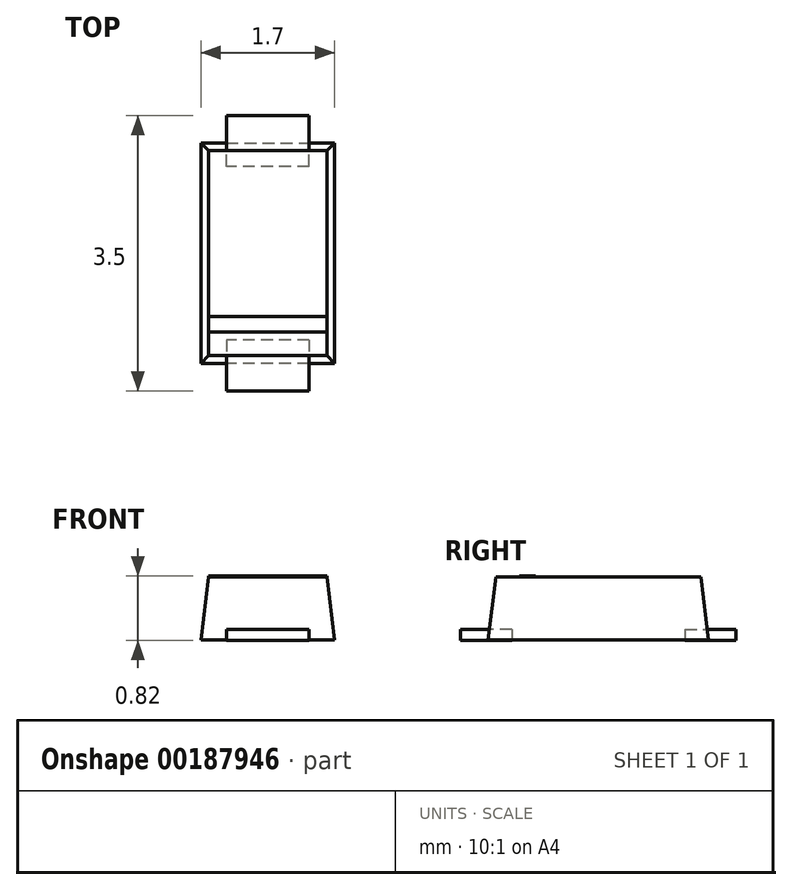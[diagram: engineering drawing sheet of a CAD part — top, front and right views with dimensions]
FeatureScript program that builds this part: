
annotation { "Feature Type Name" : "Feature", "Feature Type Description" : "" }
export const myFeature = defineFeature(function(context is Context, id is Id, definition is map)
    precondition{}
    {
        {
            var Q0;
            Q0=qCreatedBy(makeId("Top.planeOp"),FACE);
            var sketch = newSketch(context, id + "F0", { "sketchPlane" : qUnion([Q0])});
            skLineSegment(sketch, "E0.bottom", {"start": v(0.85, -1.4) * mm, "end": v(-0.85, -1.4) * mm});
            skLineSegment(sketch, "E0.top", {"start": v(0.85, 1.4) * mm, "end": v(-0.85, 1.4) * mm});
            skLineSegment(sketch, "E0.left", {"start": v(0.85, -1.4) * mm, "end": v(0.85, 1.4) * mm});
            skLineSegment(sketch, "E0.right", {"start": v(-0.85, -1.4) * mm, "end": v(-0.85, 1.4) * mm});
            skPoint(sketch, "E0.middle", {"position": v(0, 0) * mm});
            skSolve(sketch);
        }
        {
            var Q0;
            Q0=qSketchRegion(id+"F0",true);
            extrude(context, id + "F1", {"entities" : qUnion([Q0]), "depth" : 0.8 * mm, "hasDraft" : true, "draftAngle" : 7 * degree, "draftPullDirection" : true});
        }
        {
            var Q0;
            Q0=qCreatedBy(makeId("Top.planeOp"),FACE);
            var sketch = newSketch(context, id + "F2", { "sketchPlane" : qUnion([Q0])});
            skLineSegment(sketch, "E1.bottom", {"start": v(0.52, 1.1) * mm, "end": v(-0.53, 1.1) * mm});
            skLineSegment(sketch, "E1.top", {"start": v(0.53, 1.75) * mm, "end": v(-0.52, 1.75) * mm});
            skLineSegment(sketch, "E1.left", {"start": v(0.52, 1.1) * mm, "end": v(0.52, 1.75) * mm});
            skLineSegment(sketch, "E1.right", {"start": v(-0.53, 1.1) * mm, "end": v(-0.53, 1.75) * mm});
            skPoint(sketch, "E1.middle", {"position": v(0, 1.43) * mm});
            skPoint(sketch, "E2.MirrorP", {"position": v(0, -1.43) * mm});
            skLineSegment(sketch, "E3.MirrorCS", {"start": v(-0.52, -1.1) * mm, "end": v(-0.52, -1.75) * mm});
            skLineSegment(sketch, "E4.MirrorCS", {"start": v(0.53, -1.1) * mm, "end": v(0.53, -1.75) * mm});
            skLineSegment(sketch, "E5.MirrorCS", {"start": v(0.52, -1.1) * mm, "end": v(-0.53, -1.1) * mm});
            skLineSegment(sketch, "E6.MirrorCS", {"start": v(0.53, -1.75) * mm, "end": v(-0.52, -1.75) * mm});
            skSolve(sketch);
        }
        {
            var Q0;
            Q0=qSketchRegion(id+"F2",true);
            extrude(context, id + "F3", {"entities" : qUnion([Q0]), "depth" : 0.13 * mm, "hasSecondDirection" : true, "secondDirectionOppositeDirection" : true, "secondDirectionDepth" : 0.01 * mm});
        }
        {
            var Q0;
            Q0=makeQuery(id+"F1.opExtrude","CAP_FACE",FACE,{"disambiguationData":[OSD([sQuery(id+"F0.wireOp",EDGE,"E0.bottom"),sQuery(id+"F0.wireOp",EDGE,"E0.top"),sQuery(id+"F0.wireOp",EDGE,"E0.left"),sQuery(id+"F0.wireOp",EDGE,"E0.right")])],"isStart":false});
            var sketch = newSketch(context, id + "F4", { "sketchPlane" : qUnion([Q0])});
            skLineSegment(sketch, "E7.bottom", {"start": v(-0.75, -1) * mm, "end": v(0.75, -1) * mm});
            skLineSegment(sketch, "E7.top", {"start": v(-0.75, -0.8) * mm, "end": v(0.75, -0.8) * mm});
            skLineSegment(sketch, "E7.left", {"start": v(-0.75, -1) * mm, "end": v(-0.75, -0.8) * mm});
            skLineSegment(sketch, "E7.right", {"start": v(0.75, -1) * mm, "end": v(0.75, -0.8) * mm});
            skSolve(sketch);
        }
        {
            var Q0;
            Q0=qSketchRegion(id+"F4",true);
            extrude(context, id + "F5", {"entities" : qUnion([Q0]), "depth" : 0.01 * mm});
        }
    });
